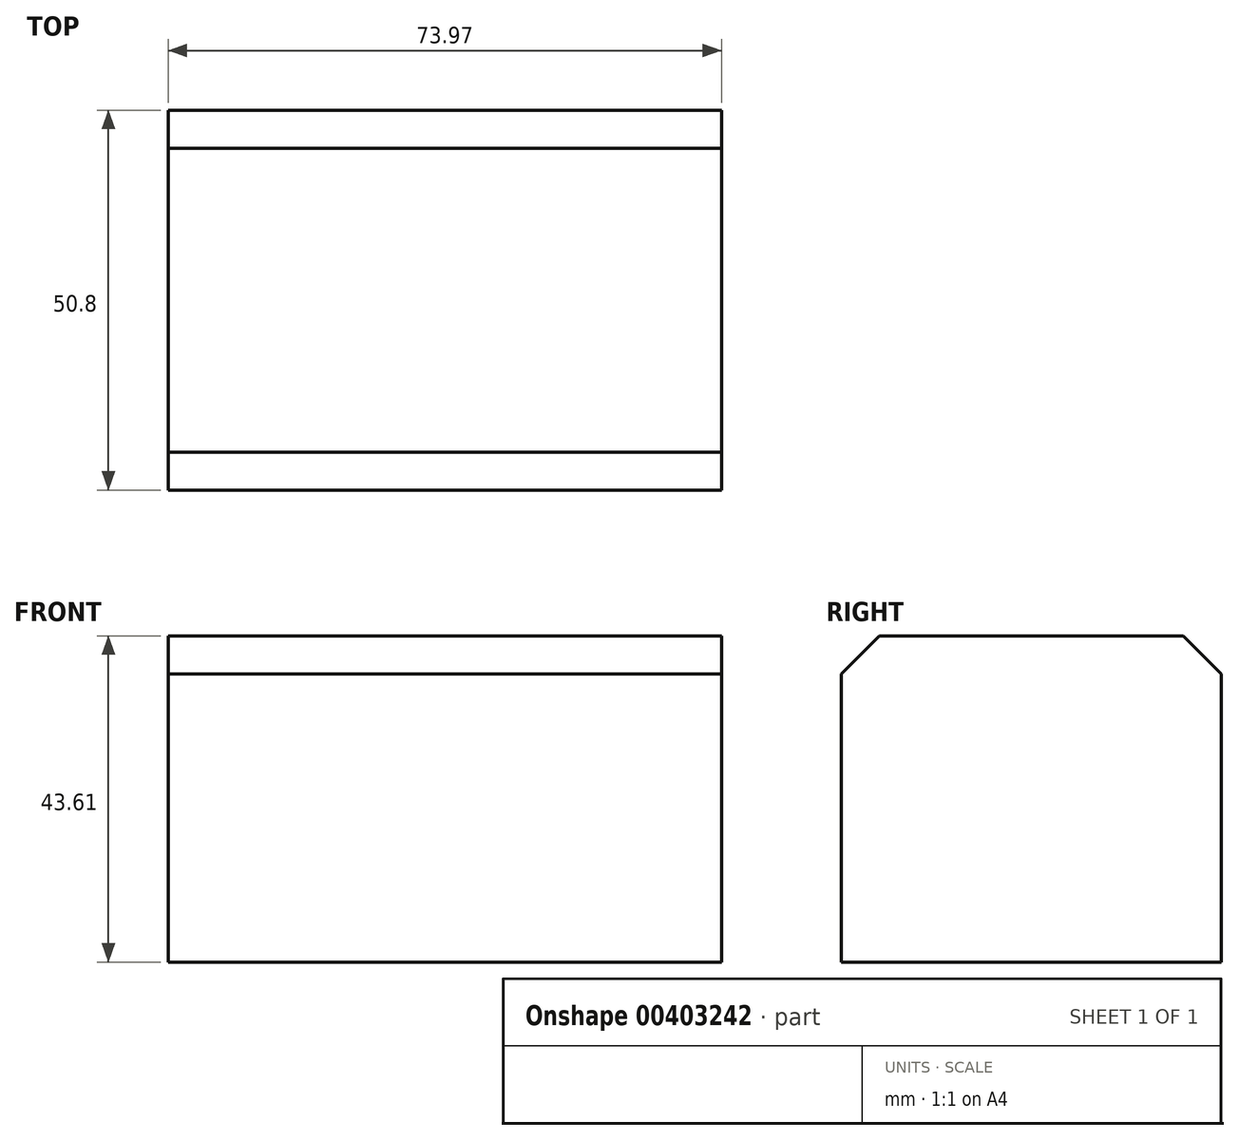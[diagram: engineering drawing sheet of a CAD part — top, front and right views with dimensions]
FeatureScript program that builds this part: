
annotation { "Feature Type Name" : "Feature", "Feature Type Description" : "" }
export const myFeature = defineFeature(function(context is Context, id is Id, definition is map)
    precondition{}
    {
        {
            var Q0;
            Q0=qCreatedBy(makeId("Front.planeOp"),FACE);
            var sketch = newSketch(context, id + "F0", { "sketchPlane" : qUnion([Q0])});
            skLineSegment(sketch, "E0.bottom", {"start": v(-38.02, 20.48) * mm, "end": v(35.95, 20.48) * mm});
            skLineSegment(sketch, "E0.top", {"start": v(-38.02, -23.13) * mm, "end": v(35.95, -23.13) * mm});
            skLineSegment(sketch, "E0.left", {"start": v(-38.02, 20.48) * mm, "end": v(-38.02, -23.13) * mm});
            skLineSegment(sketch, "E0.right", {"start": v(35.95, 20.48) * mm, "end": v(35.95, -23.13) * mm});
            skSolve(sketch);
        }
        {
            var Q0;
            Q0 = qSketchRegion(id + "F0", true);
            extrude(context, id + "F1", {"entities" : qUnion([Q0]), "depth" : 25.4 * mm});
        }
        {
            var Q0;
            Q0=makeQuery(id+"F1.opExtrude","CAP_FACE",FACE,{"disambiguationData":[OSD([sQuery(id+"F0.wireOp",EDGE,"E0.bottom"),sQuery(id+"F0.wireOp",EDGE,"E0.top"),sQuery(id+"F0.wireOp",EDGE,"E0.left"),sQuery(id+"F0.wireOp",EDGE,"E0.right")])],"isStart":false});
            extrude(context, id + "F2", {"entities" : qUnion([Q0]), "operationType" : NewBodyOperationType.ADD, "depth" : 25.4 * mm});
        }
        {
            var Q0;
            Q0=makeQuery(id+"F1.opExtrude","CAP_EDGE",EDGE,{"disambiguationData":[OSD([sQuery(id+"F0.wireOp",EDGE,"E0.bottom")])],"isStart":true});
            chamfer(context, id + "F3", {"entities" : qUnion([Q0]), "width" : 5.08 * mm, "tangentPropagation" : true});
        }
        {
            var Q0;
            Q0=makeQuery(id+"F2.opExtrude","CAP_EDGE",EDGE,{"disambiguationData":[OSD([sQuery(id+"F0.wireOp",EDGE,"E0.bottom")])],"isStart":false});
            chamfer(context, id + "F4", {"entities" : qUnion([Q0]), "width" : 5.08 * mm, "tangentPropagation" : true});
        }
    });
